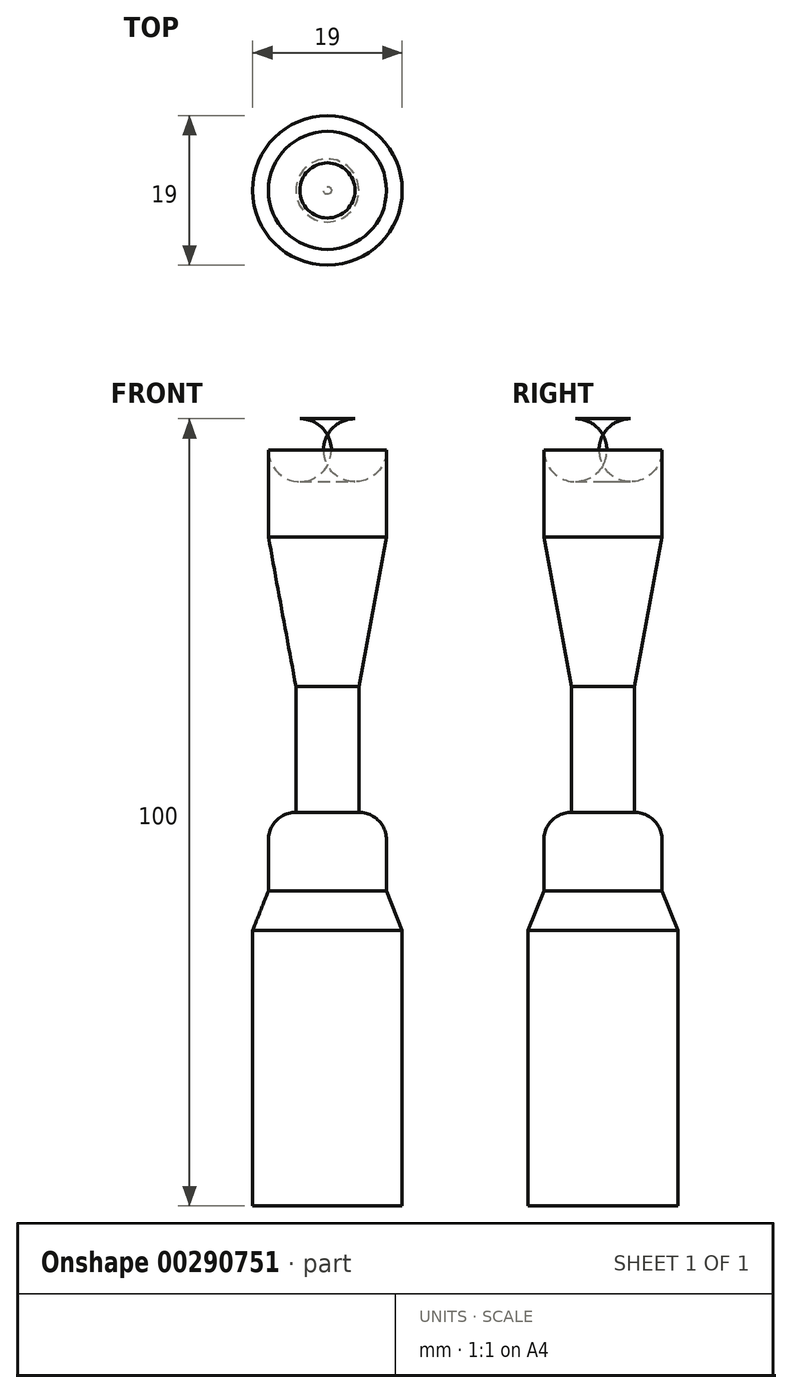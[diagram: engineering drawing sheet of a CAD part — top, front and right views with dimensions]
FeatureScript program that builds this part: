
annotation { "Feature Type Name" : "Feature", "Feature Type Description" : "" }
export const myFeature = defineFeature(function(context is Context, id is Id, definition is map)
    precondition{}
    {
        {
            var Q0;
            Q0=qCreatedBy(makeId("Front.planeOp"),FACE);
            var sketch = newSketch(context, id + "F0", { "sketchPlane" : qUnion([Q0])});
            skLineSegment(sketch, "E0", {"start": v(0, 0) * mm, "end": v(3.5, 0) * mm});
            skArc(sketch, "E1", {"start": v(7.5, -4) * mm, "mid": v(6.33, -1.17) * mm, "end": v(3.5, 0) * mm});
            skLineSegment(sketch, "E2", {"start": v(7.5, -4) * mm, "end": v(7.5, -15) * mm});
            skLineSegment(sketch, "E3", {"start": v(7.5, -15) * mm, "end": v(4, -34) * mm});
            skLineSegment(sketch, "E4", {"start": v(4, -34) * mm, "end": v(4, -50) * mm});
            skArc(sketch, "E5", {"start": v(7.5, -53.5) * mm, "mid": v(6.47, -51.03) * mm, "end": v(4, -50) * mm});
            skLineSegment(sketch, "E6", {"start": v(7.5, -53.5) * mm, "end": v(7.5, -60) * mm});
            skLineSegment(sketch, "E7", {"start": v(7.5, -60) * mm, "end": v(9.5, -65) * mm});
            skLineSegment(sketch, "E8", {"start": v(9.5, -65) * mm, "end": v(9.5, -100) * mm});
            skLineSegment(sketch, "E9", {"start": v(9.5, -100) * mm, "end": v(0, -100) * mm});
            skLineSegment(sketch, "E10", {"start": v(0, -100) * mm, "end": v(0, 0) * mm});
            skSolve(sketch);
        }
        {
            var Q0;
            Q0=makeQuery(id+"F0.imprint","IMPRINT",FACE,{"disambiguationData":[TD([[makeQuery(id+"F0.imprint","IMPRINT",EDGE,{"derivedFrom":sQuery(id+"F0.wireOp",EDGE,"E0")}),-1.0]])]});
            var Q1;
            Q1=sQuery(id+"F0.wireOp",EDGE,"E10");
            revolve(context, id + "F1", {"entities" : qUnion([Q0]), "axis" : qUnion([Q1]), "revolveType" : RevolveType.FULL});
        }
    });
